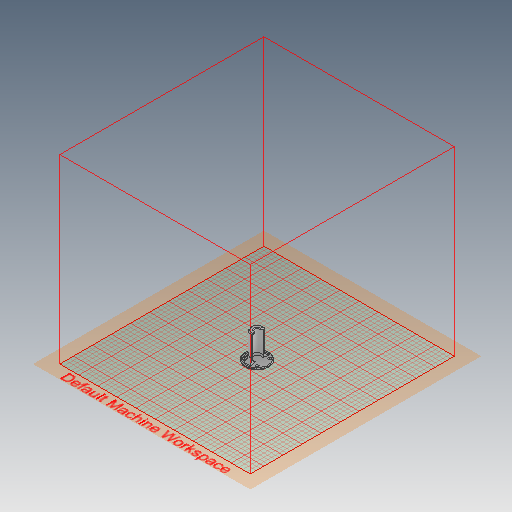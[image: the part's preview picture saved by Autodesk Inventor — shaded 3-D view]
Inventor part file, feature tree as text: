
AUTODESK INVENTOR PART (.ipt)
format: ipt  version: 2021 (Build 250183000, 183)  size: 442,880 bytes
history: native  units: mm
features: sketch x3, extrude x2, revolve x1, fillet x1
ambient origin geometry x8: Origin, YZ Plane, XZ Plane, XY Plane, X Axis, Y Axis, Z Axis, Center Point
bodies: Solid1 (feature_tree)
feature tree (7):
  extrude  "Extrusion1"  Depth=6.5mm
  revolve  "Revolution1"  Angle=360.0deg
  fillet  "Fillet1"  Radius=3.0mm
  extrude  "Extrusion2"  Depth=8.0mm
  sketch  "Sketch1"  dims[d0=53.0mm d1=6.5mm]
  sketch  "Sketch2"  dims[d2=20.0mm d3=40.0mm d5=360.0deg d7=3.0mm d8=0.0mm]
  sketch  "Sketch3"  dims[d9=45.0deg d10=12.0mm d11=6.85mm d12=2.0mm d13=55.0mm d14=3.0mm d15=34.906585mm d16=8.0mm d17=3.0mm d18=3.0mm d19=2.0mm d21=40.0mm d23=360.0deg d25=8.0mm d26=0.0mm d27=12.0mm d28=1.5mm]
